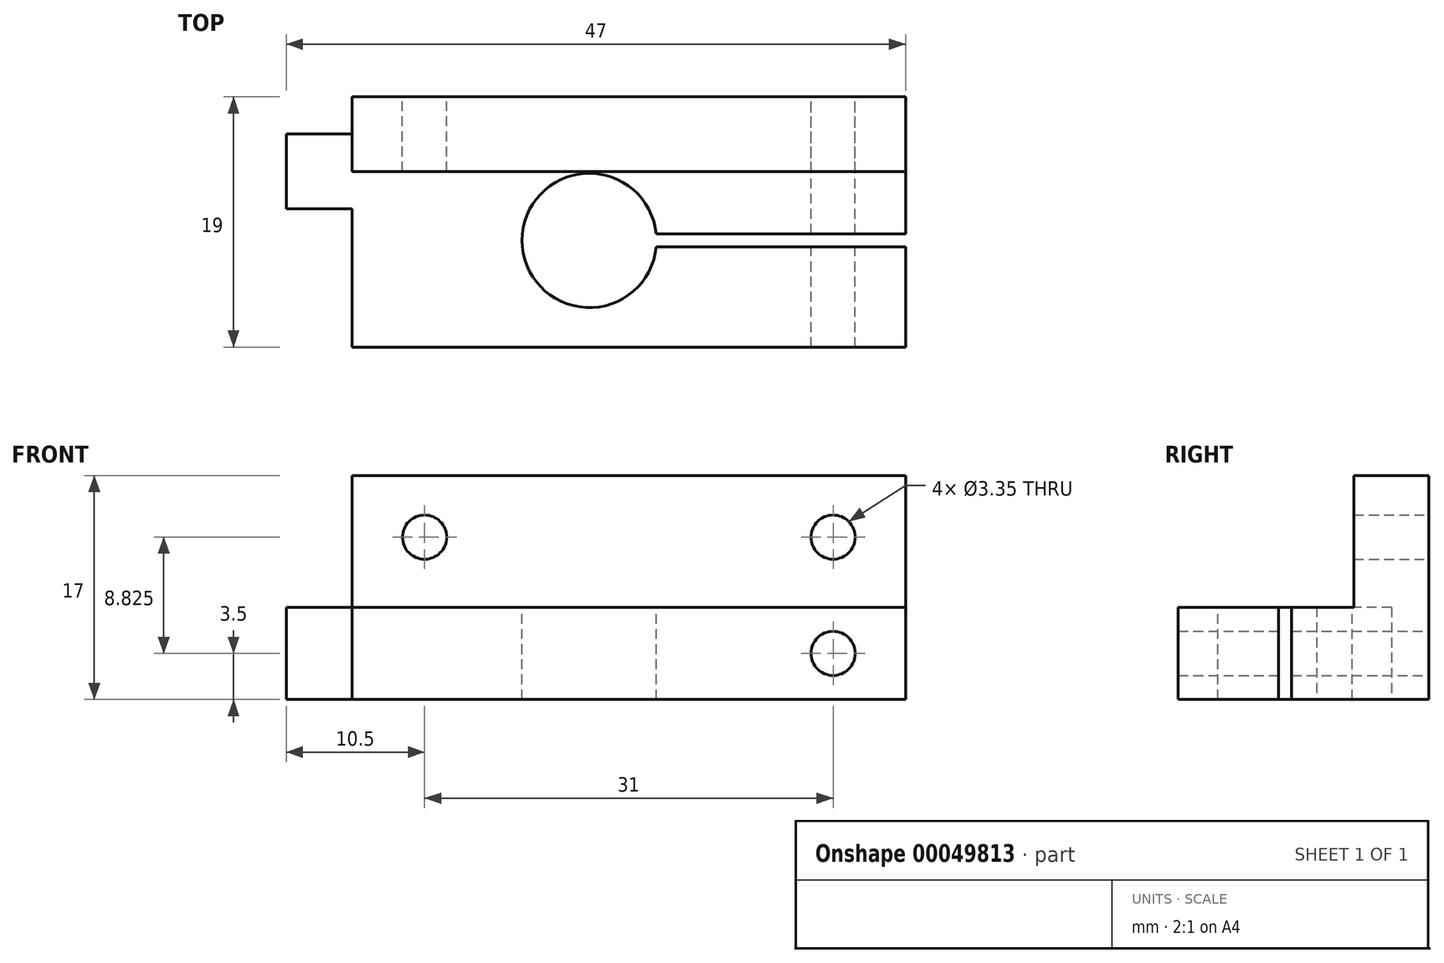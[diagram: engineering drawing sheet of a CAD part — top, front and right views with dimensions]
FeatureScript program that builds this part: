
annotation { "Feature Type Name" : "Feature", "Feature Type Description" : "" }
export const myFeature = defineFeature(function(context is Context, id is Id, definition is map)
    precondition{}
    {
        {
            var Q0;
            Q0=qCreatedBy(makeId("Top.planeOp"),FACE);
            var sketch = newSketch(context, id + "F0", { "sketchPlane" : qUnion([Q0])});
            skLineSegment(sketch, "E0.bottom", {"start": v(0, 0) * mm, "end": v(42, 0) * mm});
            skLineSegment(sketch, "E0.top", {"start": v(0, 17) * mm, "end": v(42, 17) * mm});
            skLineSegment(sketch, "E0.left", {"start": v(0, 0) * mm, "end": v(0, 17) * mm});
            skLineSegment(sketch, "E0.right", {"start": v(42, 0) * mm, "end": v(42, 17) * mm});
            skSolve(sketch);
        }
        {
            var Q0;
            Q0=qSketchRegion(id+"F0",true);
            extrude(context, id + "F1", {"entities" : qUnion([Q0]), "depth" : 7 * mm});
        }
        {
            var Q0;
            Q0=makeQuery(id+"F1.opExtrude","CAP_FACE",FACE,{"disambiguationData":[OSD([sQuery(id+"F0.wireOp",EDGE,"E0.bottom"),sQuery(id+"F0.wireOp",EDGE,"E0.top"),sQuery(id+"F0.wireOp",EDGE,"E0.left"),sQuery(id+"F0.wireOp",EDGE,"E0.right")])],"isStart":false});
            var sketch = newSketch(context, id + "F2", { "sketchPlane" : qUnion([Q0])});
            skCircle(sketch, "E1", {"center": v(18, 6.1) * mm, "radius": 5.1 * mm});
            skLineSegment(sketch, "E2", {"start": v(18, 6.1) * mm, "end": v(42, 6.1) * mm});
            skLineSegment(sketch, "E3", {"start": v(42, 6.1) * mm, "end": v(42, 5.6) * mm});
            skLineSegment(sketch, "E4", {"start": v(42, 5.6) * mm, "end": v(23.08, 5.6) * mm});
            skLineSegment(sketch, "E5", {"start": v(42, 6.1) * mm, "end": v(42, 6.6) * mm});
            skLineSegment(sketch, "E6", {"start": v(42, 6.6) * mm, "end": v(23.08, 6.6) * mm});
            skSolve(sketch);
        }
        {
            var Q0;
            Q0=makeQuery(id+"F1.opExtrude","SWEPT_FACE",FACE,{"disambiguationData":[OSD([sQuery(id+"F0.wireOp",EDGE,"E0.top")])]});
            var sketch = newSketch(context, id + "F3", { "sketchPlane" : qUnion([Q0])});
            skCircle(sketch, "E7", {"center": v(-36.5, 3.5) * mm, "radius": 1.68 * mm});
            skLineSegment(sketch, "E8", {"start": v(-36.5, 3.5) * mm, "end": v(-42, 3.5) * mm});
            skSolve(sketch);
        }
        {
            var Q0;
            Q0=qSketchRegion(id+"F3",true);
            extrude(context, id + "F4", {"entities" : qUnion([Q0]), "operationType" : NewBodyOperationType.REMOVE, "oppositeDirection" : true, "depth" : 25 * mm});
        }
        {
            var Q0;
            Q0=makeQuery(id+"F1.opExtrude","CAP_FACE",FACE,{"disambiguationData":[OSD([sQuery(id+"F0.wireOp",EDGE,"E0.bottom"),sQuery(id+"F0.wireOp",EDGE,"E0.top"),sQuery(id+"F0.wireOp",EDGE,"E0.left"),sQuery(id+"F0.wireOp",EDGE,"E0.right")])],"isStart":false});
            var sketch = newSketch(context, id + "F5", { "sketchPlane" : qUnion([Q0])});
            skLineSegment(sketch, "E9.bottom", {"start": v(0, 17) * mm, "end": v(42, 17) * mm});
            skLineSegment(sketch, "E9.top", {"start": v(0, 11.33) * mm, "end": v(42, 11.33) * mm});
            skLineSegment(sketch, "E9.left", {"start": v(0, 17) * mm, "end": v(0, 11.33) * mm});
            skLineSegment(sketch, "E9.right", {"start": v(42, 17) * mm, "end": v(42, 11.33) * mm});
            skSolve(sketch);
        }
        {
            var Q0;
            Q0=makeQuery(id+"F5.imprint","IMPRINT",FACE,{"disambiguationData":[TD([[makeQuery(id+"F5.imprint","IMPRINT",EDGE,{"derivedFrom":sQuery(id+"F5.wireOp",EDGE,"E9.bottom")}),-1.0]])]});
            extrude(context, id + "F6", {"entities" : qUnion([Q0]), "operationType" : NewBodyOperationType.ADD, "depth" : 10 * mm});
        }
        {
            var Q0;
            Q0=makeQuery(id+"F6.boolean.opBoolean","MERGE",FACE,{"derivedFrom":[makeQuery(id+"F1.opExtrude","SWEPT_FACE",FACE,{"disambiguationData":[OSD([sQuery(id+"F0.wireOp",EDGE,"E0.top")])]}),makeQuery(id+"F6.opExtrude","SWEPT_FACE",FACE,{"disambiguationData":[OSD([sQuery(id+"FFFDCbTcivKPk1C_1.wireOp",EDGE,"d29ae964-e38a-46b3-8ff4-cadffaec6662.bottom")])]})]});
            var sketch = newSketch(context, id + "F7", { "sketchPlane" : qUnion([Q0])});
            skPoint(sketch, "E10", {"position": v(-36.5, 3.5) * mm});
            skCircle(sketch, "E11", {"center": v(-36.5, 12.33) * mm, "radius": 1.68 * mm});
            skCircle(sketch, "E12", {"center": v(-5.5, 12.33) * mm, "radius": 1.68 * mm});
            skSolve(sketch);
        }
        {
            var Q0;
            Q0=qSketchRegion(id+"F7",true);
            extrude(context, id + "F8", {"entities" : qUnion([Q0]), "operationType" : NewBodyOperationType.REMOVE, "oppositeDirection" : true, "depth" : 25 * mm});
        }
        {
            var Q0;
            Q0=qSketchRegion(id+"F2",true);
            extrude(context, id + "F9", {"entities" : qUnion([Q0]), "operationType" : NewBodyOperationType.REMOVE, "oppositeDirection" : true, "depth" : 25 * mm});
        }
        {
            var Q0;
            Q0=makeQuery(id+"F6.boolean.opBoolean","MERGE",FACE,{"derivedFrom":[makeQuery(id+"F1.opExtrude","SWEPT_FACE",FACE,{"disambiguationData":[OSD([sQuery(id+"F0.wireOp",EDGE,"E0.left")])]}),makeQuery(id+"F6.opExtrude","SWEPT_FACE",FACE,{"disambiguationData":[OSD([sQuery(id+"F5.wireOp",EDGE,"E9.left")])]})]});
            var sketch = newSketch(context, id + "F10", { "sketchPlane" : qUnion([Q0])});
            skLineSegment(sketch, "E13.bottom", {"start": v(-14.2, 7) * mm, "end": v(-8.5, 7) * mm});
            skLineSegment(sketch, "E13.top", {"start": v(-14.2, 0) * mm, "end": v(-8.5, 0) * mm});
            skLineSegment(sketch, "E13.left", {"start": v(-14.2, 7) * mm, "end": v(-14.2, 0) * mm});
            skLineSegment(sketch, "E13.right", {"start": v(-8.5, 7) * mm, "end": v(-8.5, 0) * mm});
            skSolve(sketch);
        }
        {
            var Q0;
            Q0=qSketchRegion(id+"F10",true);
            extrude(context, id + "F11", {"entities" : qUnion([Q0]), "operationType" : NewBodyOperationType.ADD, "depth" : 5 * mm});
        }
        {
            var Q0;
            Q0=makeQuery(id+"F1.opExtrude","SWEPT_FACE",FACE,{"disambiguationData":[OSD([sQuery(id+"F0.wireOp",EDGE,"E0.bottom")])]});
            extrude(context, id + "F12", {"entities" : qUnion([Q0]), "operationType" : NewBodyOperationType.ADD, "depth" : 2 * mm});
        }
    });
